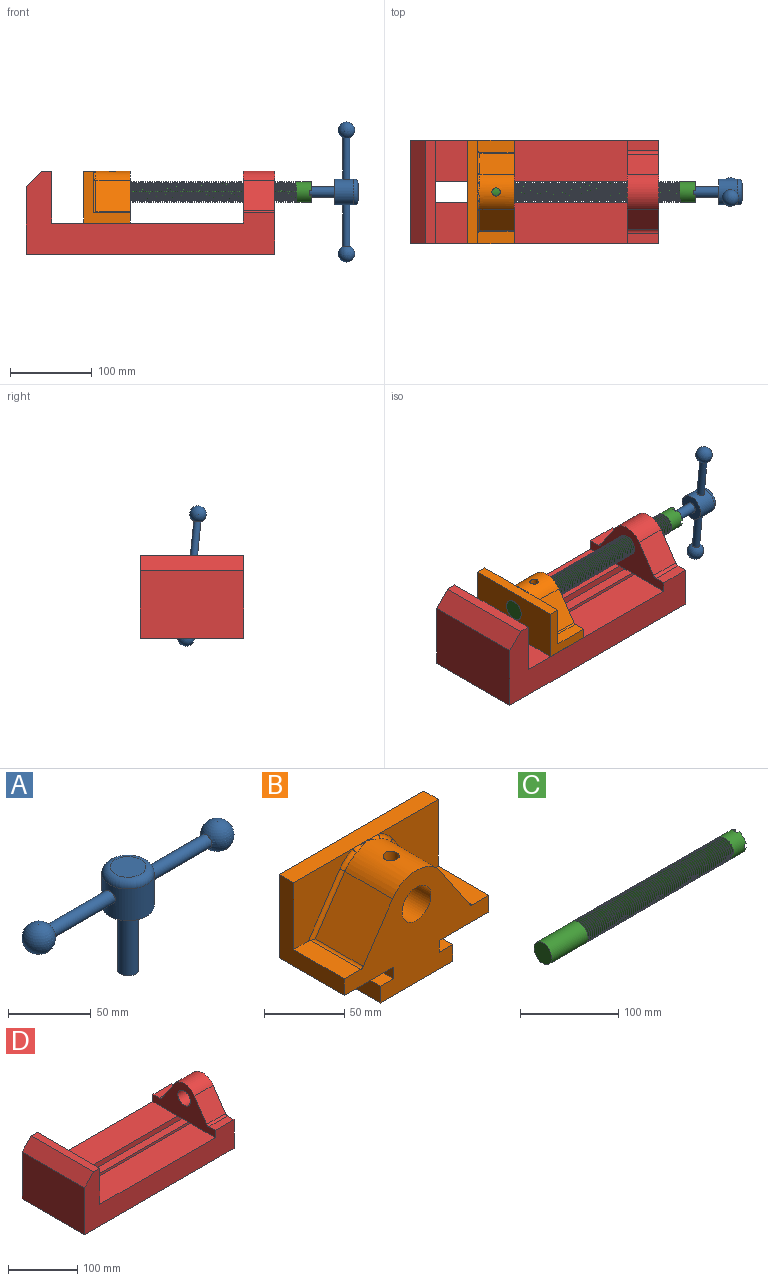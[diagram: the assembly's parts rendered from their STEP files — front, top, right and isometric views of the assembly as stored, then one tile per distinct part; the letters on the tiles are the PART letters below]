
ASSEMBLY  parts=4 mates=3
PART A: 10 faces, bbox 172.7x34.4x76.2 mm
  f0: cylinder r=4.45mm len=51.82mm, axis (-1,0,0), area 1438.5mm2, adj f1,f8
  f1: cylinder r=15.88mm len=31.75mm, axis (0,0,-1), area 2218.2mm2, adj f0,f3,f7,f9
  f2: plane 21.59x21.59mm, normal (0,0,1), area 366.1mm2, adj f9
  f3: plane 31.75x31.75mm, normal (0,0,-1), area 665.1mm2, adj f1,f4
  f4: cylinder r=6.35mm len=47.63mm, axis (0,0,1), area 1900.2mm2, adj f3,f5
  f5: plane 12.7x12.7mm, normal (0,0,-1), area 126.7mm2, adj f4
  f6: sphere r=10.16mm, area 1231.8mm2, adj f7
  f7: cylinder r=4.45mm len=51.82mm, axis (-1,0,0), area 1438.5mm2, adj f1,f6
  f8: sphere r=10.16mm, area 1231.8mm2, adj f0
  f9: torus R=10.79mm, axis (0,0,1), area 703.4mm2, adj f1,f2
PART B: 31 faces, bbox 127x57.2x89 mm
  f0: cylinder r=12.7mm len=57.15mm, axis (0,1,0), area 4477.6mm2, adj f17,f20,f22
  f1: plane 41.91x38.43mm, normal (0.83,0,0.56), area 1939.2mm2, adj f2,f17,f24,f26
  f2: cylinder r=25.4mm len=44.45mm, axis (0,1,0), area 2026.4mm2, adj f1,f3,f17,f22,f23,f25,f29,f30
  f3: plane 41.91x38.43mm, normal (-0.83,0,0.56), area 1939.2mm2, adj f2,f17,f27,f28
  f4: plane 44.49x14.56mm, normal (0,0,1), area 645.2mm2, adj f5,f17,f21,f27,f28
  f5: plane 63.5x57.15mm, normal (-1,0,0), area 1371mm2, adj f4,f6,f17,f19,f20,f21
  f6: plane 57.15x43.35mm, normal (0,0,-1), area 2477.2mm2, adj f5,f7,f17,f20
  f7: plane 57.15x8.89mm, normal (-1,0,0), area 508.1mm2, adj f6,f8,f17,f20
  f8: plane 57.15x11.6mm, normal (0,0,1), area 662.7mm2, adj f7,f9,f17,f20
  f9: plane 57.15x12.7mm, normal (-1,0,0), area 725.8mm2, adj f8,f10,f17,f20
  f10: plane 63.5x57.15mm, normal (0,0,-1), area 3629mm2, adj f9,f11,f17,f20
  f11: plane 57.15x12.7mm, normal (1,0,0), area 725.8mm2, adj f10,f12,f17,f20
  f12: plane 57.15x11.6mm, normal (0,0,1), area 662.7mm2, adj f11,f13,f17,f20
  f13: plane 57.15x8.89mm, normal (1,0,0), area 508.1mm2, adj f12,f14,f17,f20
  f14: plane 57.15x43.35mm, normal (0,0,-1), area 2477.2mm2, adj f13,f15,f17,f20
  f15: plane 63.5x57.15mm, normal (1,0,0), area 1371mm2, adj f14,f16,f17,f18,f19,f20
  f16: plane 44.49x14.56mm, normal (0,0,1), area 645.2mm2, adj f15,f17,f18,f24,f26
  f17: plane 127x85.09mm, normal (0,-1,0), area 5323.1mm2, adj f0,f1,f2,f3,f4,f5,f6,f7
  f18: plane 51.86x50.8mm, normal (0,-1,0), area 1530.4mm2, adj f15,f16,f19,f25,f26
  f19: plane 127x12.7mm, normal (0,0,1), area 1612.9mm2, adj f5,f15,f18,f20,f21,f23,f30
  f20: plane 127x85.09mm, normal (0,1,0), area 8722.6mm2, adj f0,f5,f6,f7,f8,f9,f10,f11
  f21: plane 51.86x50.8mm, normal (0,-1,0), area 1530.4mm2, adj f4,f5,f19,f28,f29
  f22: cylinder r=5.08mm len=13.76mm, axis (0,0,1), area 413.9mm2, adj f0,f2
  f23: bspline ~12.24x2.8mm, area 20.9mm2, adj f2,f19,f25
  f24: cylinder r=2.54mm len=44.02mm, axis (0,-1,0), area 106.9mm2, adj f1,f16,f17,f26
  f25: torus R=27.94mm, axis (0,-1,0), area 57.8mm2, adj f2,f18,f23,f26
  f26: cylinder r=2.54mm len=42.38mm, axis (-0.56,0,0.83), area 191.1mm2, adj f1,f16,f18,f24,f25
  f27: cylinder r=2.54mm len=44.02mm, axis (0,-1,0), area 106.9mm2, adj f3,f4,f17,f28
  f28: cylinder r=2.54mm len=42.38mm, axis (-0.56,0,-0.83), area 191.1mm2, adj f3,f4,f21,f27,f29
  f29: torus R=27.94mm, axis (0,-1,0), area 57.8mm2, adj f2,f21,f28,f30
  f30: bspline ~12.24x2.8mm, area 20.9mm2, adj f2,f19,f29
PART C: 99 faces, bbox 279.4x29.3x26.1 mm
  f0: cylinder r=12.7mm len=54.33mm, axis (-1,0,0), area 4198.4mm2, adj f1,f75,f94,f96,f98
  f1: cylinder r=12.7mm len=25.4mm, axis (-1,0,0), area 22.5mm2, adj f0,f2,f96,f98
  f2: cylinder r=12.7mm len=25.4mm, axis (-1,0,0), area 19.1mm2, adj f1,f3,f96,f98
  f3: cylinder r=12.7mm len=25.4mm, axis (-1,0,0), area 18.2mm2, adj f2,f4,f96,f98
  f4: cylinder r=12.7mm len=25.4mm, axis (-1,0,0), area 19.8mm2, adj f3,f5,f96,f98
  f5: cylinder r=12.7mm len=25.4mm, axis (-1,0,0), area 22.1mm2, adj f4,f6,f96,f98
  f6: cylinder r=12.7mm len=25.4mm, axis (-1,0,0), area 21.3mm2, adj f5,f7,f96,f98
  f7: cylinder r=12.7mm len=25.4mm, axis (-1,0,0), area 20.7mm2, adj f6,f8,f96,f98
  f8: cylinder r=12.7mm len=25.4mm, axis (-1,0,0), area 19.4mm2, adj f7,f9,f96,f98
  f9: cylinder r=12.7mm len=25.4mm, axis (-1,0,0), area 22.2mm2, adj f8,f10,f96,f98
  f10: cylinder r=12.7mm len=25.4mm, axis (-1,0,0), area 21.5mm2, adj f9,f11,f96,f98
  f11: cylinder r=12.7mm len=25.4mm, axis (-1,0,0), area 19.3mm2, adj f10,f12,f96,f98
  f12: cylinder r=12.7mm len=25.4mm, axis (-1,0,0), area 18.5mm2, adj f11,f13,f96,f98
  f13: cylinder r=12.7mm len=25.4mm, axis (-1,0,0), area 20mm2, adj f12,f14,f96,f98
  f14: cylinder r=12.7mm len=25.4mm, axis (-1,0,0), area 22.5mm2, adj f13,f15,f96,f98
  f15: cylinder r=12.7mm len=25.4mm, axis (-1,0,0), area 21.2mm2, adj f14,f16,f96,f98
  f16: cylinder r=12.7mm len=25.4mm, axis (-1,0,0), area 19.1mm2, adj f15,f17,f96,f98
  f17: cylinder r=12.7mm len=25.4mm, axis (-1,0,0), area 20.9mm2, adj f16,f18,f96,f98
  f18: cylinder r=12.7mm len=25.4mm, axis (-1,0,0), area 20.7mm2, adj f17,f19,f96,f98
  f19: cylinder r=12.7mm len=25.4mm, axis (-1,0,0), area 19.5mm2, adj f18,f20,f96,f98
  f20: cylinder r=12.7mm len=25.4mm, axis (-1,0,0), area 23.4mm2, adj f19,f21,f96,f98
  f21: cylinder r=12.7mm len=25.4mm, axis (-1,0,0), area 18.3mm2, adj f20,f22,f96,f98
  f22: cylinder r=12.7mm len=25.4mm, axis (-1,0,0), area 21.8mm2, adj f21,f23,f96,f98
  f23: cylinder r=12.7mm len=25.4mm, axis (-1,0,0), area 20.6mm2, adj f22,f24,f96,f98
  f24: cylinder r=12.7mm len=25.4mm, axis (-1,0,0), area 22.2mm2, adj f23,f25,f96,f98
  f25: cylinder r=12.7mm len=25.4mm, axis (-1,0,0), area 22.1mm2, adj f24,f26,f96,f98
  f26: cylinder r=12.7mm len=25.4mm, axis (-1,0,0), area 20.6mm2, adj f25,f27,f96,f98
  f27: cylinder r=12.7mm len=25.4mm, axis (-1,0,0), area 20.9mm2, adj f26,f28,f96,f98
  f28: cylinder r=12.7mm len=25.4mm, axis (-1,0,0), area 21mm2, adj f27,f29,f96,f98
  f29: cylinder r=12.7mm len=25.4mm, axis (-1,0,0), area 20.5mm2, adj f28,f30,f96,f98
  f30: cylinder r=12.7mm len=25.4mm, axis (-1,0,0), area 19.2mm2, adj f29,f31,f96,f98
  f31: cylinder r=12.7mm len=25.4mm, axis (-1,0,0), area 20.5mm2, adj f30,f32,f96,f98
  f32: cylinder r=12.7mm len=25.4mm, axis (-1,0,0), area 18.4mm2, adj f31,f33,f96,f98
  f33: cylinder r=12.7mm len=25.4mm, axis (-1,0,0), area 21mm2, adj f32,f34,f96,f98
  f34: cylinder r=12.7mm len=25.4mm, axis (-1,0,0), area 21mm2, adj f33,f35,f96,f98
  f35: cylinder r=12.7mm len=25.4mm, axis (-1,0,0), area 21mm2, adj f34,f36,f96,f98
  f36: cylinder r=12.7mm len=25.4mm, axis (-1,0,0), area 20.6mm2, adj f35,f37,f96,f98
  f37: cylinder r=12.7mm len=25.4mm, axis (-1,0,0), area 19.5mm2, adj f36,f38,f96,f98
  f38: cylinder r=12.7mm len=25.4mm, axis (-1,0,0), area 21.3mm2, adj f37,f39,f96,f98
  f39: cylinder r=12.7mm len=25.4mm, axis (-1,0,0), area 19.5mm2, adj f38,f40,f96,f98
  f40: cylinder r=12.7mm len=25.4mm, axis (-1,0,0), area 19.7mm2, adj f39,f41,f96,f98
  f41: cylinder r=12.7mm len=25.4mm, axis (-1,0,0), area 20mm2, adj f40,f42,f96,f98
  f42: cylinder r=12.7mm len=25.4mm, axis (-1,0,0), area 19.6mm2, adj f41,f43,f96,f98
  f43: cylinder r=12.7mm len=25.4mm, axis (-1,0,0), area 20.5mm2, adj f42,f44,f96,f98
  f44: cylinder r=12.7mm len=25.4mm, axis (-1,0,0), area 21.6mm2, adj f43,f45,f96,f98
  f45: cylinder r=12.7mm len=25.4mm, axis (-1,0,0), area 21.6mm2, adj f44,f46,f96,f98
  f46: cylinder r=12.7mm len=25.4mm, axis (-1,0,0), area 22.3mm2, adj f45,f47,f96,f98
  f47: cylinder r=12.7mm len=25.4mm, axis (-1,0,0), area 20.6mm2, adj f46,f48,f96,f98
  f48: cylinder r=12.7mm len=25.4mm, axis (-1,0,0), area 22.4mm2, adj f47,f49,f96,f98
  f49: cylinder r=12.7mm len=25.4mm, axis (-1,0,0), area 21.1mm2, adj f48,f50,f96,f98
  f50: cylinder r=12.7mm len=25.4mm, axis (-1,0,0), area 22.1mm2, adj f49,f51,f96,f98
  f51: cylinder r=12.7mm len=25.4mm, axis (-1,0,0), area 17.7mm2, adj f50,f52,f96,f98
  f52: cylinder r=12.7mm len=25.4mm, axis (-1,0,0), area 19mm2, adj f51,f53,f96,f98
  f53: cylinder r=12.7mm len=25.4mm, axis (-1,0,0), area 22mm2, adj f52,f54,f96,f98
  f54: cylinder r=12.7mm len=25.4mm, axis (-1,0,0), area 21.3mm2, adj f53,f55,f96,f98
  f55: cylinder r=12.7mm len=25.4mm, axis (-1,0,0), area 19.9mm2, adj f54,f56,f96,f98
  f56: cylinder r=12.7mm len=25.4mm, axis (-1,0,0), area 20.9mm2, adj f55,f57,f96,f98
  f57: cylinder r=12.7mm len=25.4mm, axis (-1,0,0), area 21.2mm2, adj f56,f58,f96,f98
  f58: cylinder r=12.7mm len=25.4mm, axis (-1,0,0), area 21.9mm2, adj f57,f59,f96,f98
  f59: cylinder r=12.7mm len=25.4mm, axis (-1,0,0), area 19.4mm2, adj f58,f60,f96,f98
  f60: cylinder r=12.7mm len=25.4mm, axis (-1,0,0), area 19.2mm2, adj f59,f61,f96,f98
  f61: cylinder r=12.7mm len=25.4mm, axis (-1,0,0), area 19.2mm2, adj f60,f62,f96,f98
  f62: cylinder r=12.7mm len=25.4mm, axis (-1,0,0), area 21.3mm2, adj f61,f63,f96,f98
  f63: cylinder r=12.7mm len=25.4mm, axis (-1,0,0), area 21.6mm2, adj f62,f64,f96,f98
  f64: cylinder r=12.7mm len=25.4mm, axis (-1,0,0), area 19.9mm2, adj f63,f65,f96,f98
  f65: cylinder r=12.7mm len=25.4mm, axis (-1,0,0), area 21mm2, adj f64,f66,f96,f98
  f66: cylinder r=12.7mm len=25.4mm, axis (-1,0,0), area 18.6mm2, adj f65,f67,f96,f98
  f67: cylinder r=12.7mm len=25.4mm, axis (-1,0,0), area 18.5mm2, adj f66,f68,f96,f98
  f68: cylinder r=12.7mm len=25.4mm, axis (-1,0,0), area 19mm2, adj f67,f69,f96,f98
  f69: cylinder r=12.7mm len=25.4mm, axis (-1,0,0), area 20.4mm2, adj f68,f70,f96,f98
  f70: cylinder r=12.7mm len=25.4mm, axis (-1,0,0), area 20.9mm2, adj f69,f71,f96,f98
  f71: cylinder r=12.7mm len=25.4mm, axis (-1,0,0), area 19.8mm2, adj f70,f72,f96,f98
  f72: cylinder r=12.7mm len=25.4mm, axis (-1,0,0), area 20mm2, adj f71,f73,f96,f98
  f73: cylinder r=12.7mm len=25.4mm, axis (-1,0,0), area 21.1mm2, adj f72,f74,f96,f98
  f74: cylinder r=12.7mm len=25.4mm, axis (-1,0,0), area 1483.3mm2, adj f73,f76,f77,f78,f79,f80,f81,f82
  f75: plane 25.4x25.4mm, normal (-1,0,0), area 506.7mm2, adj f0
  f76: plane 9.9x9.9mm, normal (1,0,0), area 62.3mm2, adj f74,f83,f89,f92
  f77: plane 9.9x9.9mm, normal (1,0,0), area 62.3mm2, adj f74,f86,f90,f92
  f78: plane 9.9x9.9mm, normal (1,0,0), area 62.3mm2, adj f74,f80,f87,f92
  f79: plane 9.9x9.9mm, normal (1,0,0), area 62.3mm2, adj f74,f81,f84,f92
  f80: plane 6.62x2.54mm, normal (0,1,0), area 16.8mm2, adj f74,f78,f82,f92
  f81: plane 6.62x2.54mm, normal (0,-1,0), area 16.8mm2, adj f74,f79,f82,f92
  f82: plane 6.88x5.08mm, normal (1,0,0), area 32.7mm2, adj f74,f80,f81,f92
  f83: plane 6.62x2.54mm, normal (0,0,-1), area 16.8mm2, adj f74,f76,f85,f92
  f84: plane 6.62x2.54mm, normal (0,0,1), area 16.8mm2, adj f74,f79,f85,f92
  f85: plane 6.88x5.08mm, normal (1,0,0), area 32.7mm2, adj f74,f83,f84,f92
  f86: plane 6.62x2.54mm, normal (0,0,-1), area 16.8mm2, adj f74,f77,f88,f92
  f87: plane 6.62x2.54mm, normal (0,0,1), area 16.8mm2, adj f74,f78,f88,f92
  f88: plane 6.88x5.08mm, normal (1,0,0), area 32.7mm2, adj f74,f86,f87,f92
  f89: plane 6.62x2.54mm, normal (0,-1,0), area 16.8mm2, adj f74,f76,f91,f92
  f90: plane 6.62x2.54mm, normal (0,1,0), area 16.8mm2, adj f74,f77,f91,f92
  f91: plane 6.88x5.08mm, normal (1,0,0), area 32.7mm2, adj f74,f89,f90,f92
  f92: cylinder r=6.35mm len=19.05mm, axis (1,0,0), area 707mm2, adj f76,f77,f78,f79,f80,f81,f82,f83
  f93: plane 12.7x12.7mm, normal (1,0,0), area 126.7mm2, adj f92
  f94: plane 2.54x2.17mm, normal (0.04,-0.54,0.84), area 4.8mm2, adj f0,f96,f97,f98
  f95: plane 2.54x2.54mm, normal (-0.04,0,1), area 4.8mm2, adj f74,f96,f97,f98
  f96: bspline ~208.79x29.29mm, area 14006.8mm2, adj f0,f1,f2,f3,f4,f5,f6,f7
  f97: bspline ~209.42x23.44mm, area 6032.6mm2, adj f94,f95,f96,f98
  f98: bspline ~208.79x29.3mm, area 13995.4mm2, adj f0,f1,f2,f3,f4,f5,f6,f7
PART D: 30 faces, bbox 304.8x127x101.6 mm
  f0: plane 234.95x50.8mm, normal (0,0,1), area 11935.5mm2, adj f4,f6,f9,f23
  f1: plane 127x82.55mm, normal (-1,0,0), area 10483.8mm2, adj f2,f8,f9,f10
  f2: plane 304.8x127mm, normal (0,0,-1), area 31774.1mm2, adj f1,f3,f6,f9,f10,f18,f27
  f3: plane 127x101.6mm, normal (1,0,0), area 7547.1mm2, adj f2,f9,f10,f11,f12,f13,f14,f15
  f4: plane 127x63.5mm, normal (-1,0,0), area 4160mm2, adj f0,f5,f9,f10,f11,f12,f13,f14
  f5: plane 234.95x50.8mm, normal (0,0,1), area 11935.5mm2, adj f4,f6,f10,f22
  f6: plane 127x101.6mm, normal (1,0,0), area 9516.1mm2, adj f0,f2,f5,f7,f9,f10,f18,f19
  f7: plane 127x12.7mm, normal (0,0,1), area 1612.9mm2, adj f6,f8,f9,f10
  f8: plane 127x19.05mm, normal (-0.71,0,0.71), area 3421.5mm2, adj f1,f7,f9,f10
  f9: plane 304.8x101.6mm, normal (0,-1,0), area 13931.4mm2, adj f0,f1,f2,f3,f4,f6,f7,f8
  f10: plane 304.8x101.6mm, normal (0,1,0), area 13931.4mm2, adj f1,f2,f3,f4,f5,f6,f7,f8
  f11: plane 38.1x13.17mm, normal (0,0,1), area 501.6mm2, adj f3,f4,f10,f29
  f12: cylinder r=25.4mm len=42.19mm, axis (1,0,0), area 1896.6mm2, adj f3,f4,f13,f15
  f13: plane 38.1x37.3mm, normal (0,0.83,0.56), area 1711.3mm2, adj f3,f4,f12,f29
  f14: plane 38.1x13.17mm, normal (0,0,1), area 501.6mm2, adj f3,f4,f9,f28
  f15: plane 38.1x37.3mm, normal (0,-0.83,0.56), area 1711.3mm2, adj f3,f4,f12,f28
  f16: cylinder r=12.7mm len=38.1mm, axis (1,0,0), area 3040.2mm2, adj f3,f4
  f17: plane 38.1x25.4mm, normal (0,0,-1), area 967.7mm2, adj f3,f4,f22,f23
  f18: plane 273.05x16.51mm, normal (0,-1,0), area 4508.1mm2, adj f2,f3,f6,f19
  f19: plane 273.05x19.05mm, normal (0,0,1), area 5201.6mm2, adj f3,f6,f18,f20
  f20: plane 273.05x12.7mm, normal (0,-1,0), area 3467.7mm2, adj f3,f6,f19,f21
  f21: plane 273.05x19.05mm, normal (0,0,-1), area 5201.6mm2, adj f3,f6,f20,f22
  f22: plane 273.05x8.89mm, normal (0,-1,0), area 2427.4mm2, adj f3,f5,f6,f17,f21
  f23: plane 273.05x8.89mm, normal (0,1,0), area 2427.4mm2, adj f0,f3,f6,f17,f24
  f24: plane 273.05x19.05mm, normal (0,0,-1), area 5201.6mm2, adj f3,f6,f23,f25
  f25: plane 273.05x12.7mm, normal (0,1,0), area 3467.7mm2, adj f3,f6,f24,f26
  f26: plane 273.05x19.05mm, normal (0,0,1), area 5201.6mm2, adj f3,f6,f25,f27
  f27: plane 273.05x16.51mm, normal (0,1,0), area 4508.1mm2, adj f2,f3,f6,f26
  f28: cylinder r=5.08mm len=38.1mm, axis (-1,0,0), area 189.7mm2, adj f3,f4,f14,f15
  f29: cylinder r=5.08mm len=38.1mm, axis (-1,0,0), area 189.7mm2, adj f3,f4,f11,f13
PLACE A rot(axis=(0.05,1,0.05),90.1deg) t=(138.85,0,76.2)mm
PLACE B rot(axis=(0,0,1),90deg) t=(-170.72,0,76.2)mm
PLACE C rot(axis=(1,0,0),95.6deg) t=(-310.42,0,76.2)mm
PLACE D at identity fixed
MATE fastened C.f0 <-> A.f1  axis (1,0,0) through (330.93,0,76.2)mm
MATE slider D.f6 <-> B.f20  axis (1,0,0) through (31.75,0,101.6)mm
MATE revolute B.f0 <-> C.f0  axis (-1,0,0) through (70.58,0,76.2)mm
